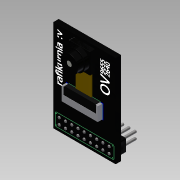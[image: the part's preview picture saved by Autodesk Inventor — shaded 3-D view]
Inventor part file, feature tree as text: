
AUTODESK INVENTOR PART (.ipt)
format: ipt  version: 2015 SP1 (Build 190203100, 203)  size: 400,384 bytes
history: native  units: mm
features: extrude x12, sketch x6, projected_geometry x4, fillet x3
ambient origin geometry x8: Origin, YZ Plane, XZ Plane, XY Plane, X Axis, Y Axis, Z Axis, Center Point
bodies: Solid1 (feature_tree)
feature tree (25):
  sketch  "Sketch1"  dims[d0=24.32mm d1=35.9mm]
  extrude  "Extrusion1"  Depth=35.9mm
  extrude  "Extrusion2"  Depth=8.05mm
  extrude  "Extrusion3"  Depth=1.0mm
  extrude  "Extrusion4"  Depth=7.88mm
  extrude  "Extrusion5"  Depth=6.05mm
  extrude  "Extrusion6"  Depth=0.25mm
  extrude  "Extrusion7"  Depth=1.0mm
  extrude  "Extrusion8"  TaperAngle=90.0deg  [1 undecoded]
  extrude  "Extrusion9"  Depth=0.25mm
  extrude  "Extrusion10"  Depth=1.0mm
  fillet  "Fillet1"  [1 undecoded]
  fillet  "Fillet2"  Radius=5.33mm
  fillet  "Fillet3"  Radius=2.432mm
  extrude  "Extrusion11"  Depth=0.1mm
  extrude  "Extrusion12"  Depth=1.0mm
  sketch  "Sketch4"  dims[d6=8.05mm d7=7.88mm]
  sketch  "Sketch5"  dims[d8=6.84mm d9=6.05mm]
  sketch  "Sketch6"  dims[d10=8.63mm d13=0.25mm d14=1.0mm d15=90.0deg d16=0.25mm d17=1.0mm d18=90.0deg d19=5.33mm d21=2.432mm d22=2.432mm d23=1.0mm d24=90.0mm d26=2.432mm d27=20.0mm d29=2.432mm d32=22.96mm d33=4.98mm d34=2.09mm d35=0.0mm d36=4.05mm d37=0.0mm d38=5.81mm d39=0.0mm d40=8.1mm d41=0.0mm d42=2.5mm d43=0.0mm d44=3.88mm d45=0.0mm d46=2.09mm d47=0.0mm d48=2.62mm d49=0.0mm d50=8.2mm d51=0.0mm d52=2.5mm d53=0.0mm d54=0.25mm d55=0.5mm d56=0.125mm d60=0.7mm d61=0.7mm d62=2.41mm d63=0.1mm d64=0.0mm d65=2.0mm d66=0.1mm d67=0.0mm d68=0.1mm]
  sketch  "Sketch2"  dims[d2=8.22mm d3=8.05mm]
  sketch  "Sketch3"  dims[d4=1.0mm d5=8.05mm]
  projected_geometry  "Projected Loop2"
  projected_geometry  "Projected Loop3"
  projected_geometry  "Projected Loop4"
  projected_geometry  "Projected Loop5"
note: 2 required parameter values undecoded (feature->parameter linkage not recoverable at this tier; creation-order binding heuristic only, values carry confidence <= 0.55)
